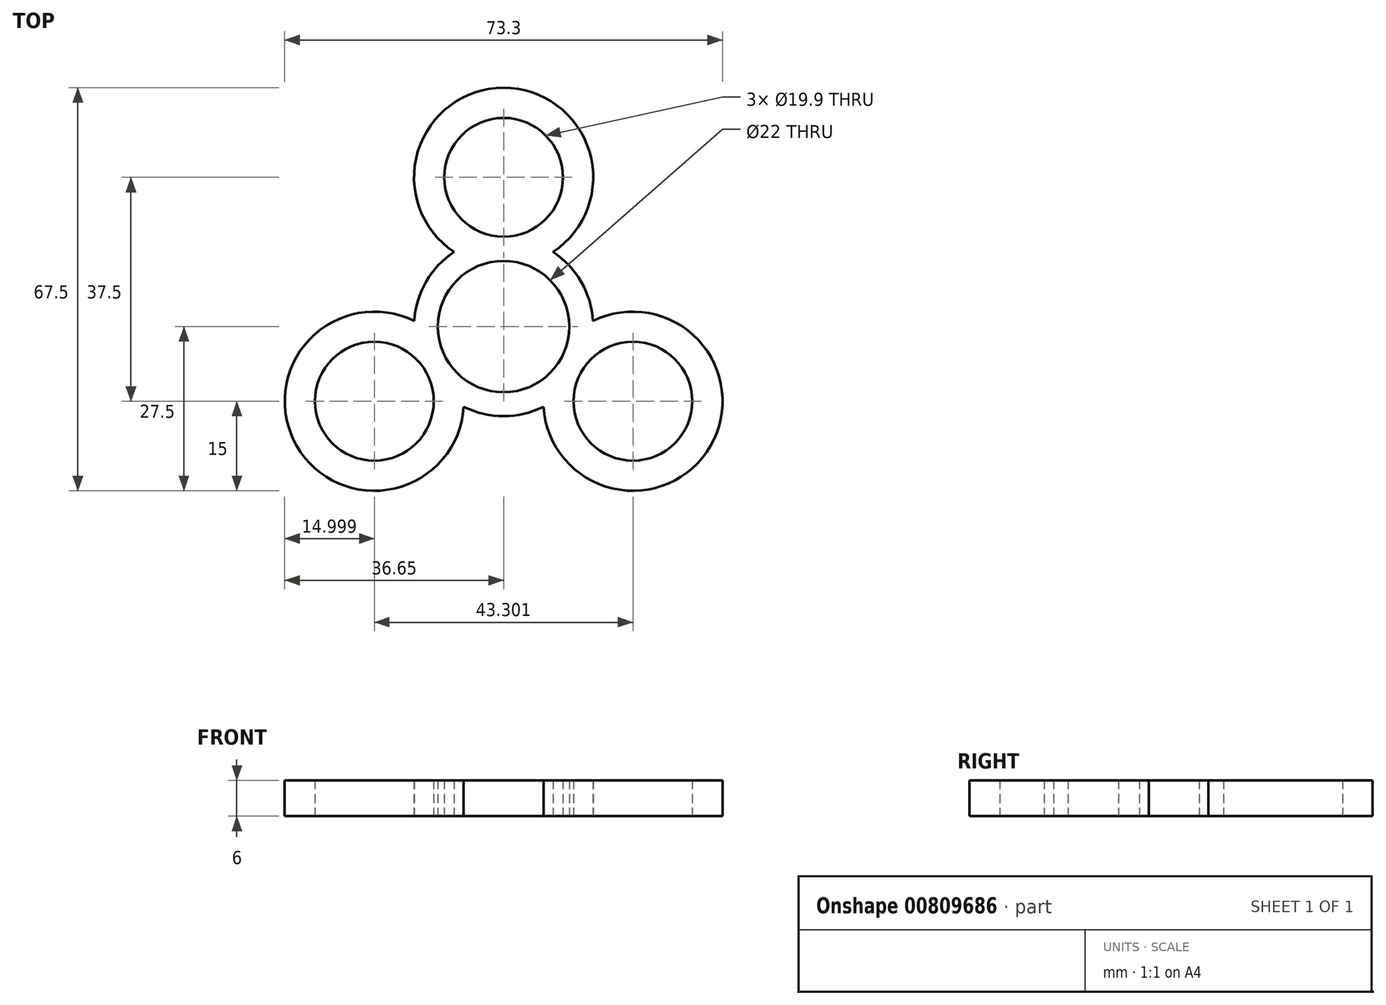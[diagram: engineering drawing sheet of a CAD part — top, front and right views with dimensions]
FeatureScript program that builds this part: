
annotation { "Feature Type Name" : "Feature", "Feature Type Description" : "" }
export const myFeature = defineFeature(function(context is Context, id is Id, definition is map)
    precondition{}
    {
        {
            var Q0;
            Q0=qCreatedBy(makeId("Top.planeOp"),FACE);
            var sketch = newSketch(context, id + "F0", { "sketchPlane" : qUnion([Q0])});
            skArc(sketch, "E0", {"start": v(9.53, 5.5) * mm, "mid": v(0, 11) * mm, "end": v(-9.53, 5.5) * mm});
            skArc(sketch, "E1", {"start": v(13, 7.5) * mm, "mid": v(10.93, 10.27) * mm, "end": v(8.3, 12.5) * mm});
            skCircle(sketch, "E2", {"center": v(0, 25) * mm, "radius": 9.95 * mm});
            skArc(sketch, "E3", {"start": v(8.3, 12.5) * mm, "mid": v(0, 40) * mm, "end": v(-8.3, 12.5) * mm});
            skArc(sketch, "E4.trimOffspring", {"start": v(-8.3, 12.5) * mm, "mid": v(-10.93, 10.27) * mm, "end": v(-13, 7.5) * mm});
            skArc(sketch, "E5.1.1", {"start": v(-9.53, 5.5) * mm, "mid": v(-9.53, -5.5) * mm, "end": v(0, -11) * mm});
            skArc(sketch, "E5.1.2", {"start": v(-13, 7.5) * mm, "mid": v(-14.36, 4.33) * mm, "end": v(-14.97, 0.93) * mm});
            skCircle(sketch, "E5.1.3", {"center": v(-21.65, -12.5) * mm, "radius": 9.95 * mm});
            skArc(sketch, "E5.1.4", {"start": v(-14.97, 0.93) * mm, "mid": v(-34.64, -20) * mm, "end": v(-6.68, -13.43) * mm});
            skArc(sketch, "E5.1.5", {"start": v(-6.68, -13.43) * mm, "mid": v(-3.43, -14.6) * mm, "end": v(0, -15) * mm});
            skArc(sketch, "E5.2.1", {"start": v(0, -11) * mm, "mid": v(9.53, -5.5) * mm, "end": v(9.53, 5.5) * mm});
            skArc(sketch, "E5.2.2", {"start": v(0, -15) * mm, "mid": v(3.43, -14.6) * mm, "end": v(6.68, -13.43) * mm});
            skCircle(sketch, "E5.2.3", {"center": v(21.65, -12.5) * mm, "radius": 9.95 * mm});
            skArc(sketch, "E5.2.4", {"start": v(6.68, -13.43) * mm, "mid": v(34.64, -20) * mm, "end": v(14.97, 0.93) * mm});
            skArc(sketch, "E5.2.5", {"start": v(14.97, 0.93) * mm, "mid": v(14.36, 4.33) * mm, "end": v(13, 7.5) * mm});
            skSolve(sketch);
        }
        {
            var Q0;
            Q0 = qSketchRegion(id + "F0", true);
            extrude(context, id + "F1", {"entities" : qUnion([Q0]), "depth" : 6 * mm, "offsetDistance" : 25 * mm});
        }
    });
